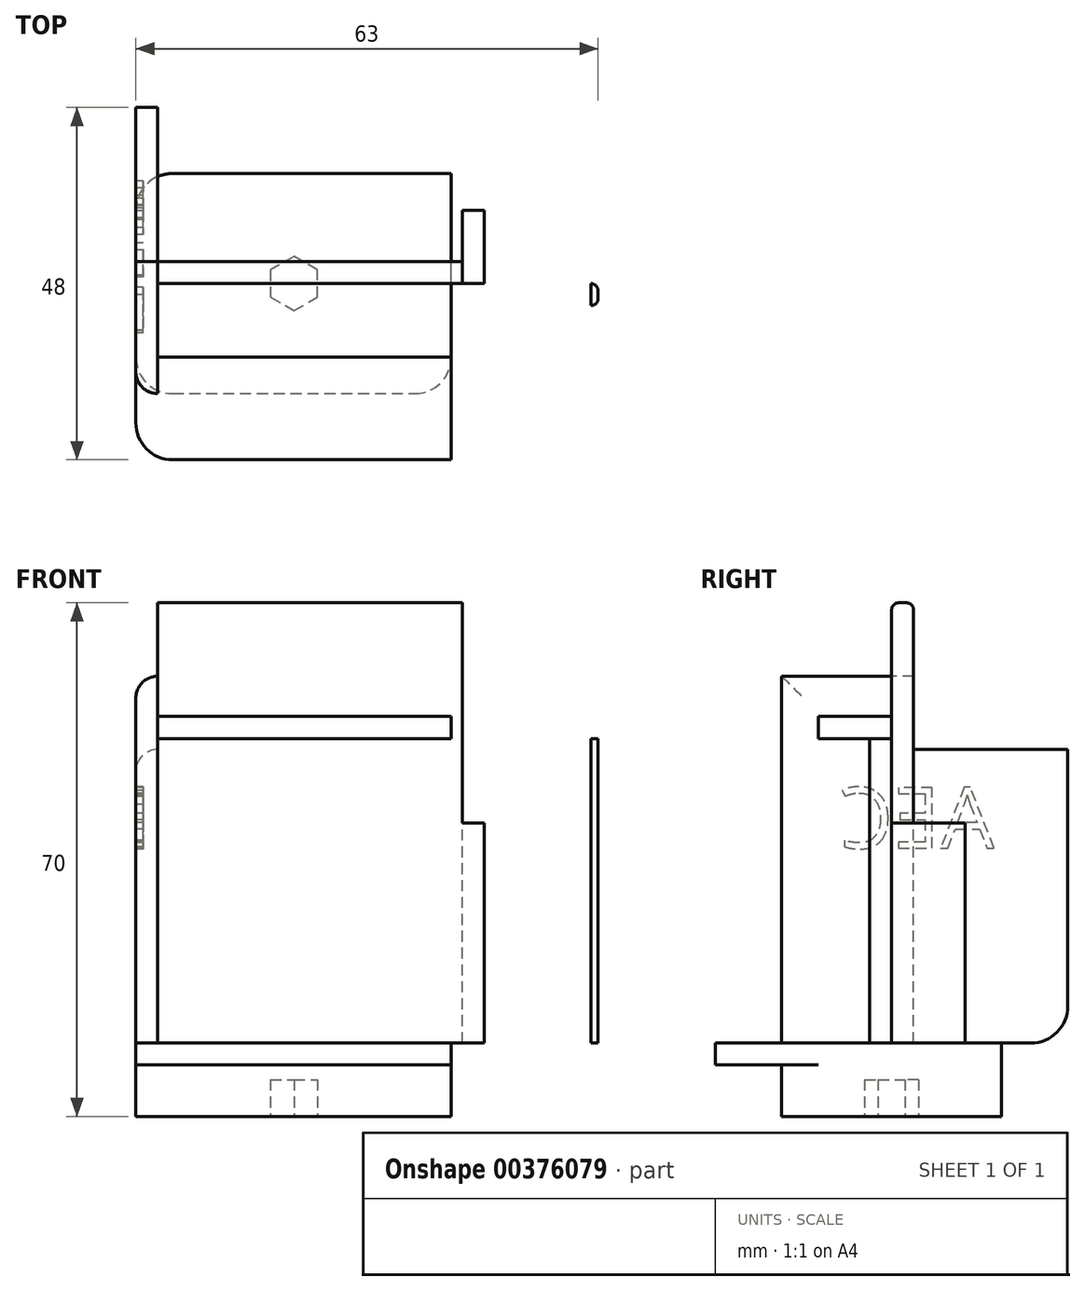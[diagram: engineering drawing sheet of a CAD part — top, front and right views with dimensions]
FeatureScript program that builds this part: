
annotation { "Feature Type Name" : "Feature", "Feature Type Description" : "" }
export const myFeature = defineFeature(function(context is Context, id is Id, definition is map)
    precondition{}
    {
        {
            var Q0;
            Q0=qCreatedBy(makeId("Front.planeOp"),FACE);
            var sketch = newSketch(context, id + "F0", { "sketchPlane" : qUnion([Q0])});
            skLineSegment(sketch, "E0.bottom", {"start": v(0, 0) * mm, "end": v(60, 0) * mm});
            skLineSegment(sketch, "E0.top", {"start": v(0, 41.5) * mm, "end": v(60, 41.5) * mm});
            skLineSegment(sketch, "E0.left", {"start": v(0, 0) * mm, "end": v(0, 41.5) * mm});
            skLineSegment(sketch, "E0.right", {"start": v(60, 0) * mm, "end": v(60, 41.5) * mm});
            skSolve(sketch);
        }
        {
            var Q0;
            Q0=makeQuery(id+"F0.imprint","IMPRINT",FACE,{"disambiguationData":[TD([[makeQuery(id+"F0.imprint","IMPRINT",EDGE,{"derivedFrom":sQuery(id+"F0.wireOp",EDGE,"E0.bottom")}),1.0]])]});
            extrude(context, id + "F1", {"entities" : qUnion([Q0]), "depth" : 3 * mm});
        }
        {
            var Q0;
            Q0=makeQuery(id+"F1.opExtrude","CAP_FACE",FACE,{"disambiguationData":[OSD([sQuery(id+"F0.wireOp",EDGE,"E0.bottom"),sQuery(id+"F0.wireOp",EDGE,"E0.top"),sQuery(id+"F0.wireOp",EDGE,"E0.left"),sQuery(id+"F0.wireOp",EDGE,"E0.right")])],"isStart":true});
            var sketch = newSketch(context, id + "F2", { "sketchPlane" : qUnion([Q0])});
            skLineSegment(sketch, "E1.bottom", {"start": v(0, 0) * mm, "end": v(-41.5, 0) * mm});
            skLineSegment(sketch, "E1.top", {"start": v(0, 60) * mm, "end": v(-41.5, 60) * mm});
            skLineSegment(sketch, "E1.left", {"start": v(0, 0) * mm, "end": v(0, 60) * mm});
            skLineSegment(sketch, "E1.right", {"start": v(-41.5, 0) * mm, "end": v(-41.5, 60) * mm});
            skSolve(sketch);
        }
        {
            var Q0;
            {var subQ0=sQuery(id+"F2.wireOp",EDGE,"E1.top");Q0=makeQuery(id+"F2.imprint","IMPRINT",FACE,{"disambiguationData":[TD([[makeQuery(id+"F2.imprint","IMPRINT",EDGE,{"derivedFrom":subQ0}),1.0]])]});}
            var Q1;
            {var subQ0=sQuery(id+"F2.wireOp",EDGE,"E1.bottom");Q1=makeQuery(id+"F2.imprint","IMPRINT",FACE,{"disambiguationData":[TD([[makeQuery(id+"F2.imprint","IMPRINT",EDGE,{"derivedFrom":subQ0}),-1.0]])]});}
            extrude(context, id + "F3", {"entities" : qUnion([Q0, Q1]), "operationType" : NewBodyOperationType.ADD, "depth" : 3 * mm});
        }
        {
            var Q0;
            Q0=makeQuery(id+"F3.boolean.opBoolean","MERGE",FACE,{"derivedFrom":[makeQuery(id+"F1.opExtrude","SWEPT_FACE",FACE,{"disambiguationData":[OSD([sQuery(id+"F0.wireOp",EDGE,"E0.left")])]}),makeQuery(id+"F3.opExtrude","SWEPT_FACE",FACE,{"disambiguationData":[OSD([sQuery(id+"F2.wireOp",EDGE,"E1.left")])]})]});
            var sketch = newSketch(context, id + "F4", { "sketchPlane" : qUnion([Q0])});
            skLineSegment(sketch, "E2", {"start": v(0, 0) * mm, "end": v(-15, 0) * mm, "construction": true});
            skLineSegment(sketch, "E3", {"start": v(-15, 0) * mm, "end": v(15, 0) * mm, "construction": true});
            skLineSegment(sketch, "E4", {"start": v(15, 0) * mm, "end": v(15, 50) * mm, "construction": true});
            skLineSegment(sketch, "E5.bottom", {"start": v(-15, 0) * mm, "end": v(15, 0) * mm});
            skLineSegment(sketch, "E5.top", {"start": v(-15, 50) * mm, "end": v(15, 50) * mm});
            skLineSegment(sketch, "E5.left", {"start": v(-15, 0) * mm, "end": v(-15, 50) * mm});
            skLineSegment(sketch, "E5.right", {"start": v(15, 0) * mm, "end": v(15, 50) * mm});
            skSolve(sketch);
        }
        {
            var Q0;
            {var subQ3=sQuery(id+"F4.wireOp",EDGE,"E5.left");Q0=makeQuery(id+"F4.imprint","IMPRINT",FACE,{"disambiguationData":[TD([[makeQuery(id+"F4.imprint","IMPRINT",EDGE,{"derivedFrom":subQ3}),-1.0]])]});}
            var Q1;
            {var subQ2=sQuery(id+"F4.wireOp",EDGE,"E5.right");Q1=makeQuery(id+"F4.imprint","IMPRINT",FACE,{"disambiguationData":[TD([[makeQuery(id+"F4.imprint","IMPRINT",EDGE,{"derivedFrom":subQ2}),1.0]])]});}
            var Q2;
            {var subQ0=sQuery(id+"F0.wireOp",EDGE,"E0.left");var subQ1=makeQuery(id+"F1.opExtrude","CAP_EDGE",EDGE,{"disambiguationData":[OSD([subQ0])],"isStart":false});Q2=makeQuery(id+"F4.imprint","IMPRINT",FACE,{"disambiguationData":[TD([[makeQuery(id+"F4.imprint","IMPRINT",EDGE,{"derivedFrom":subQ1}),1.0]])]});}
            extrude(context, id + "F5", {"entities" : qUnion([Q0, Q1, Q2]), "operationType" : NewBodyOperationType.ADD, "depth" : 3 * mm});
        }
        {
            var Q0;
            Q0=makeQuery(id+"F5.boolean.opBoolean","MERGE",FACE,{"derivedFrom":[makeQuery(id+"F3.boolean.opBoolean","MERGE",FACE,{"derivedFrom":[makeQuery(id+"F1.opExtrude","SWEPT_FACE",FACE,{"disambiguationData":[OSD([sQuery(id+"F0.wireOp",EDGE,"E0.bottom")])]}),makeQuery(id+"F3.opExtrude","SWEPT_FACE",FACE,{"disambiguationData":[OSD([sQuery(id+"F2.wireOp",EDGE,"E1.bottom")])]})]}),makeQuery(id+"F5.opExtrude","SWEPT_FACE",FACE,{"disambiguationData":[OSD([sQuery(id+"F4.wireOp",EDGE,"E5.bottom")])]})]});
            var sketch = newSketch(context, id + "F6", { "sketchPlane" : qUnion([Q0])});
            skLineSegment(sketch, "E6.bottom", {"start": v(-3, 15) * mm, "end": v(47, 15) * mm});
            skLineSegment(sketch, "E6.top", {"start": v(-3, -15) * mm, "end": v(47, -15) * mm});
            skLineSegment(sketch, "E6.left", {"start": v(-3, 15) * mm, "end": v(-3, -15) * mm});
            skLineSegment(sketch, "E6.right", {"start": v(47, 15) * mm, "end": v(47, -15) * mm});
            skSolve(sketch);
        }
        {
            var Q0;
            {var subQ0=sQuery(id+"F6.wireOp",EDGE,"E6.bottom");var subQ5=sQuery(id+"F6.wireOp",EDGE,"E6.right");var subQ6=makeQuery(id+"F6.imprint","INTERSECT",VERTEX,{"derivedFrom":[subQ0,subQ5]});Q0=makeQuery(id+"F6.imprint","IMPRINT",FACE,{"disambiguationData":[TD([[makeQuery(id+"F6.imprint","IMPRINT",EDGE,{"disambiguationData":[TD([[subQ6,-1.0]])],"derivedFrom":subQ5}),-1.0]])]});}
            var Q1;
            {var subQ0=sQuery(id+"F2.wireOp",EDGE,"E1.bottom");Q1=makeQuery(id+"F6.imprint","IMPRINT",FACE,{"disambiguationData":[TD([[makeQuery(id+"F6.imprint","IMPRINT",EDGE,{"derivedFrom":makeQuery(id+"F3.opExtrude","CAP_EDGE",EDGE,{"disambiguationData":[OSD([subQ0])],"isStart":false})}),-1.0]])]});}
            var Q2;
            {var subQ6=sQuery(id+"F6.wireOp",EDGE,"E6.left");Q2=makeQuery(id+"F6.imprint","IMPRINT",FACE,{"disambiguationData":[TD([[makeQuery(id+"F6.imprint","IMPRINT",EDGE,{"derivedFrom":subQ6}),-1.0]])]});}
            extrude(context, id + "F7", {"entities" : qUnion([Q0, Q1, Q2]), "operationType" : NewBodyOperationType.ADD, "depth" : 10 * mm});
        }
        {
            var Q0;
            Q0=makeQuery(id+"F7.boolean.opBoolean","MERGE",FACE,{"derivedFrom":[makeQuery(id+"F5.opExtrude","SWEPT_FACE",FACE,{"disambiguationData":[OSD([sQuery(id+"F4.wireOp",EDGE,"E5.right")])]}),makeQuery(id+"F7.opExtrude","SWEPT_FACE",FACE,{"disambiguationData":[OSD([sQuery(id+"F6.wireOp",EDGE,"E6.bottom")])]})]});
            var sketch = newSketch(context, id + "F8", { "sketchPlane" : qUnion([Q0])});
            skLineSegment(sketch, "E7.bottom", {"start": v(-3, 0) * mm, "end": v(47, 0) * mm});
            skLineSegment(sketch, "E7.top", {"start": v(-3, -3) * mm, "end": v(47, -3) * mm});
            skLineSegment(sketch, "E7.left", {"start": v(-3, 0) * mm, "end": v(-3, -3) * mm});
            skLineSegment(sketch, "E7.right", {"start": v(47, 0) * mm, "end": v(47, -3) * mm});
            skSolve(sketch);
        }
        {
            var Q0;
            Q0=makeQuery(id+"F8.imprint","IMPRINT",FACE,{"disambiguationData":[TD([[makeQuery(id+"F8.imprint","IMPRINT",EDGE,{"derivedFrom":sQuery(id+"F8.wireOp",EDGE,"E7.top")}),1.0]])]});
            extrude(context, id + "F9", {"entities" : qUnion([Q0]), "operationType" : NewBodyOperationType.ADD, "depth" : 9 * mm});
        }
        {
            var Q0;
            Q0=makeQuery(id+"F9.opExtrude","CAP_FACE",FACE,{"disambiguationData":[OSD([sQuery(id+"F8.wireOp",EDGE,"E7.bottom"),sQuery(id+"F8.wireOp",EDGE,"E7.top"),sQuery(id+"F8.wireOp",EDGE,"E7.left"),sQuery(id+"F8.wireOp",EDGE,"E7.right")])],"isStart":false});
            var sketch = newSketch(context, id + "F10", { "sketchPlane" : qUnion([Q0])});
            skLineSegment(sketch, "E8.bottom", {"start": v(22, -3) * mm, "end": v(47, -3) * mm});
            skLineSegment(sketch, "E8.top", {"start": v(22, 7) * mm, "end": v(47, 7) * mm});
            skLineSegment(sketch, "E8.left", {"start": v(22, -3) * mm, "end": v(22, 7) * mm});
            skLineSegment(sketch, "E8.right", {"start": v(47, -3) * mm, "end": v(47, 7) * mm});
            skSolve(sketch);
        }
        {
            var Q0;
            {var subQ0=sQuery(id+"F10.wireOp",EDGE,"E8.top");Q0=makeQuery(id+"F10.imprint","IMPRINT",FACE,{"disambiguationData":[TD([[makeQuery(id+"F10.imprint","IMPRINT",EDGE,{"derivedFrom":subQ0}),-1.0]])]});}
            var Q1;
            {var subQ0=sQuery(id+"F10.wireOp",EDGE,"E8.bottom");Q1=makeQuery(id+"F10.imprint","IMPRINT",FACE,{"disambiguationData":[TD([[makeQuery(id+"F10.imprint","IMPRINT",EDGE,{"derivedFrom":subQ0}),1.0]])]});}
            extrude(context, id + "F11", {"entities" : qUnion([Q0, Q1]), "operationType" : NewBodyOperationType.ADD, "depth" : 3 * mm});
        }
        {
            var Q0;
            Q0=makeQuery(id+"F11.opExtrude","CAP_FACE",FACE,{"disambiguationData":[OSD([sQuery(id+"F10.wireOp",EDGE,"E8.bottom"),sQuery(id+"F10.wireOp",EDGE,"E8.top"),sQuery(id+"F10.wireOp",EDGE,"E8.left"),sQuery(id+"F10.wireOp",EDGE,"E8.right")])],"isStart":false});
            var sketch = newSketch(context, id + "F12", { "sketchPlane" : qUnion([Q0])});
            skArc(sketch, "E9", {"start": v(17.11, 3.6) * mm, "mid": v(26.46, 3.05) * mm, "end": v(24.78, 12.26) * mm});
            skLineSegment(sketch, "E10", {"start": v(24.78, 12.26) * mm, "end": v(17.11, 3.6) * mm});
            skSolve(sketch);
        }
        {
            var Q0;
            {var subQ0=sQuery(id+"F12.wireOp",EDGE,"E9");var subQ1=makeQuery(id+"F11.opExtrude","CAP_EDGE",EDGE,{"disambiguationData":[OSD([sQuery(id+"F10.wireOp",EDGE,"E8.left")])],"isStart":false});var subQ2=makeQuery(id+"F12.imprint","INTERSECT",VERTEX,{"derivedFrom":[subQ1,subQ0]});Q0=makeQuery(id+"F12.imprint","IMPRINT",FACE,{"disambiguationData":[TD([[makeQuery(id+"F12.imprint","IMPRINT",EDGE,{"disambiguationData":[TD([[subQ2,-1.0]])],"derivedFrom":subQ0}),1.0]])]});}
            extrude(context, id + "F13", {"entities" : qUnion([Q0]), "operationType" : NewBodyOperationType.REMOVE, "oppositeDirection" : true, "depth" : 3 * mm});
        }
        {
            var Q0;
            Q0=makeQuery(id+"F11.boolean.opBoolean","MERGE",FACE,{"derivedFrom":[makeQuery(id+"F9.boolean.opBoolean","MERGE",FACE,{"derivedFrom":[makeQuery(id+"F7.opExtrude","SWEPT_FACE",FACE,{"disambiguationData":[OSD([sQuery(id+"F6.wireOp",EDGE,"E6.right")])]}),makeQuery(id+"F9.opExtrude","SWEPT_FACE",FACE,{"disambiguationData":[OSD([sQuery(id+"F8.wireOp",EDGE,"E7.right")])]})]}),makeQuery(id+"F11.opExtrude","SWEPT_FACE",FACE,{"disambiguationData":[OSD([sQuery(id+"F10.wireOp",EDGE,"E8.right")])]})]});
            var sketch = newSketch(context, id + "F14", { "sketchPlane" : qUnion([Q0])});
            skLineSegment(sketch, "E11.bottom", {"start": v(15, 0) * mm, "end": v(-27.93, 0) * mm});
            skLineSegment(sketch, "E11.top", {"start": v(15, -10) * mm, "end": v(-27.93, -10) * mm});
            skLineSegment(sketch, "E11.left", {"start": v(15, 0) * mm, "end": v(15, -10) * mm});
            skLineSegment(sketch, "E11.right", {"start": v(-27.93, 0) * mm, "end": v(-27.93, -10) * mm});
            skSolve(sketch);
        }
        {
            var Q0;
            {var subQ5=sQuery(id+"F14.wireOp",EDGE,"E11.left");Q0=makeQuery(id+"F14.imprint","IMPRINT",FACE,{"disambiguationData":[TD([[makeQuery(id+"F14.imprint","IMPRINT",EDGE,{"derivedFrom":subQ5}),1.0]])]});}
            var Q1;
            {var subQ3=sQuery(id+"F14.wireOp",EDGE,"E11.right");Q1=makeQuery(id+"F14.imprint","IMPRINT",FACE,{"disambiguationData":[TD([[makeQuery(id+"F14.imprint","IMPRINT",EDGE,{"derivedFrom":subQ3}),1.0]])]});}
            extrude(context, id + "F15", {"entities" : qUnion([Q0, Q1]), "operationType" : NewBodyOperationType.REMOVE, "oppositeDirection" : true, "depth" : 7 * mm});
        }
        {
            var Q0;
            Q0=makeQuery(id+"F11.boolean.opBoolean","MERGE",FACE,{"derivedFrom":[makeQuery(id+"F9.boolean.opBoolean","MERGE",FACE,{"derivedFrom":[makeQuery(id+"F7.opExtrude","SWEPT_FACE",FACE,{"disambiguationData":[OSD([sQuery(id+"F6.wireOp",EDGE,"E6.right")])]}),makeQuery(id+"F9.opExtrude","SWEPT_FACE",FACE,{"disambiguationData":[OSD([sQuery(id+"F8.wireOp",EDGE,"E7.right")])]})]}),makeQuery(id+"F11.opExtrude","SWEPT_FACE",FACE,{"disambiguationData":[OSD([sQuery(id+"F10.wireOp",EDGE,"E8.right")])]})]});
            var sketch = newSketch(context, id + "F16", { "sketchPlane" : qUnion([Q0])});
            skLineSegment(sketch, "E12.bottom", {"start": v(-31.9, 9.79) * mm, "end": v(-20.1, 9.79) * mm});
            skLineSegment(sketch, "E12.top", {"start": v(-31.9, -3.14) * mm, "end": v(-20.1, -3.14) * mm});
            skLineSegment(sketch, "E12.left", {"start": v(-31.9, 9.79) * mm, "end": v(-31.9, -3.14) * mm});
            skLineSegment(sketch, "E12.right", {"start": v(-20.1, 9.79) * mm, "end": v(-20.1, -3.14) * mm});
            skSolve(sketch);
        }
        {
            var Q0;
            {var subQ0=sQuery(id+"F10.wireOp",EDGE,"E8.right");Q0=makeQuery(id+"F16.imprint","IMPRINT",FACE,{"disambiguationData":[TD([[makeQuery(id+"F16.imprint","IMPRINT",EDGE,{"derivedFrom":makeQuery(id+"F11.opExtrude","CAP_EDGE",EDGE,{"disambiguationData":[OSD([subQ0])],"isStart":true})}),1.0]])]});}
            extrude(context, id + "F17", {"entities" : qUnion([Q0]), "operationType" : NewBodyOperationType.REMOVE, "oppositeDirection" : true, "depth" : 7 * mm});
        }
        {
            var Q0;
            Q0=makeQuery(id+"F11.opExtrude","CAP_FACE",FACE,{"disambiguationData":[OSD([sQuery(id+"F10.wireOp",EDGE,"E8.bottom"),sQuery(id+"F10.wireOp",EDGE,"E8.top"),sQuery(id+"F10.wireOp",EDGE,"E8.left"),sQuery(id+"F10.wireOp",EDGE,"E8.right")])],"isStart":false});
            var sketch = newSketch(context, id + "F18", { "sketchPlane" : qUnion([Q0])});
            skLineSegment(sketch, "E13.bottom", {"start": v(40, 7) * mm, "end": v(35.21, 7) * mm});
            skLineSegment(sketch, "E13.top", {"start": v(40, 2.28) * mm, "end": v(35.21, 2.28) * mm});
            skLineSegment(sketch, "E13.left", {"start": v(40, 7) * mm, "end": v(40, 2.28) * mm});
            skLineSegment(sketch, "E13.right", {"start": v(35.21, 7) * mm, "end": v(35.21, 2.28) * mm});
            skSolve(sketch);
        }
        {
            var Q0;
            Q0=makeQuery(id+"F18.imprint","IMPRINT",FACE,{"disambiguationData":[TD([[makeQuery(id+"F18.imprint","IMPRINT",EDGE,{"derivedFrom":sQuery(id+"F18.wireOp",EDGE,"E13.bottom")}),-1.0]])]});
            extrude(context, id + "F19", {"entities" : qUnion([Q0]), "operationType" : NewBodyOperationType.REMOVE, "oppositeDirection" : true, "depth" : 5 * mm});
        }
        {
            var Q0;
            Q0=makeQuery(id+"F1.opExtrude","SWEPT_FACE",FACE,{"disambiguationData":[OSD([sQuery(id+"F0.wireOp",EDGE,"E0.top")])]});
            var sketch = newSketch(context, id + "F20", { "sketchPlane" : qUnion([Q0])});
            skLineSegment(sketch, "E14.bottom", {"start": v(0, 0) * mm, "end": v(40, 0) * mm});
            skLineSegment(sketch, "E14.top", {"start": v(0, -10) * mm, "end": v(40, -10) * mm});
            skLineSegment(sketch, "E14.left", {"start": v(0, 0) * mm, "end": v(0, -10) * mm});
            skLineSegment(sketch, "E14.right", {"start": v(40, 0) * mm, "end": v(40, -10) * mm});
            skSolve(sketch);
        }
        {
            var Q0;
            {var subQ0=sQuery(id+"F20.wireOp",EDGE,"E14.top");Q0=makeQuery(id+"F20.imprint","IMPRINT",FACE,{"disambiguationData":[TD([[makeQuery(id+"F20.imprint","IMPRINT",EDGE,{"derivedFrom":subQ0}),1.0]])]});}
            var Q1;
            {var subQ0=sQuery(id+"F20.wireOp",EDGE,"E14.bottom");Q1=makeQuery(id+"F20.imprint","IMPRINT",FACE,{"disambiguationData":[TD([[makeQuery(id+"F20.imprint","IMPRINT",EDGE,{"derivedFrom":subQ0}),-1.0]])]});}
            extrude(context, id + "F21", {"entities" : qUnion([Q0, Q1]), "operationType" : NewBodyOperationType.ADD, "depth" : 3 * mm});
        }
        {
            var Q0;
            Q0=makeQuery(id+"F3.opExtrude","SWEPT_FACE",FACE,{"disambiguationData":[OSD([sQuery(id+"F2.wireOp",EDGE,"E1.right")])]});
            var sketch = newSketch(context, id + "F22", { "sketchPlane" : qUnion([Q0])});
            skLineSegment(sketch, "E15.bottom", {"start": v(0, 0) * mm, "end": v(10, 0) * mm});
            skLineSegment(sketch, "E15.top", {"start": v(0, 30) * mm, "end": v(10, 30) * mm});
            skLineSegment(sketch, "E15.left", {"start": v(0, 0) * mm, "end": v(0, 30) * mm});
            skLineSegment(sketch, "E15.right", {"start": v(10, 0) * mm, "end": v(10, 30) * mm});
            skSolve(sketch);
        }
        {
            var Q0;
            {var subQ3=sQuery(id+"F22.wireOp",EDGE,"E15.right");Q0=makeQuery(id+"F22.imprint","IMPRINT",FACE,{"disambiguationData":[TD([[makeQuery(id+"F22.imprint","IMPRINT",EDGE,{"derivedFrom":subQ3}),1.0]])]});}
            var Q1;
            {var subQ4=sQuery(id+"F22.wireOp",EDGE,"E15.left");Q1=makeQuery(id+"F22.imprint","IMPRINT",FACE,{"disambiguationData":[TD([[makeQuery(id+"F22.imprint","IMPRINT",EDGE,{"derivedFrom":subQ4}),-1.0]])]});}
            extrude(context, id + "F23", {"entities" : qUnion([Q0, Q1]), "operationType" : NewBodyOperationType.ADD, "depth" : 3 * mm});
        }
        {
            var Q0;
            Q0=makeQuery(id+"F7.boolean.opBoolean","MERGE",FACE,{"derivedFrom":[makeQuery(id+"F5.opExtrude","SWEPT_FACE",FACE,{"disambiguationData":[OSD([sQuery(id+"F4.wireOp",EDGE,"E5.left")])]}),makeQuery(id+"F7.opExtrude","SWEPT_FACE",FACE,{"disambiguationData":[OSD([sQuery(id+"F6.wireOp",EDGE,"E6.top")])]})]});
            var sketch = newSketch(context, id + "F24", { "sketchPlane" : qUnion([Q0])});
            skLineSegment(sketch, "E16.bottom", {"start": v(0, 50) * mm, "end": v(3, 50) * mm});
            skLineSegment(sketch, "E16.top", {"start": v(0, 0) * mm, "end": v(3, 0) * mm});
            skLineSegment(sketch, "E16.left", {"start": v(0, 50) * mm, "end": v(0, 0) * mm});
            skLineSegment(sketch, "E16.right", {"start": v(3, 50) * mm, "end": v(3, 0) * mm});
            skSolve(sketch);
        }
        {
            var Q0;
            Q0=makeQuery(id+"F24.imprint","IMPRINT",FACE,{"disambiguationData":[TD([[makeQuery(id+"F24.imprint","IMPRINT",EDGE,{"derivedFrom":sQuery(id+"F24.wireOp",EDGE,"E16.bottom")}),1.0]])]});
            extrude(context, id + "F25", {"entities" : qUnion([Q0]), "operationType" : NewBodyOperationType.ADD, "depth" : 9 * mm});
        }
        {
            var Q0;
            Q0=makeQuery(id+"F11.opExtrude","CAP_FACE",FACE,{"disambiguationData":[OSD([sQuery(id+"F10.wireOp",EDGE,"E8.bottom"),sQuery(id+"F10.wireOp",EDGE,"E8.top"),sQuery(id+"F10.wireOp",EDGE,"E8.left"),sQuery(id+"F10.wireOp",EDGE,"E8.right")])],"isStart":false});
            var sketch = newSketch(context, id + "F26", { "sketchPlane" : qUnion([Q0])});
            skLineSegment(sketch, "E17.bottom", {"start": v(27.95, 7) * mm, "end": v(22, 7) * mm});
            skLineSegment(sketch, "E17.top", {"start": v(27.95, 1.05) * mm, "end": v(22, 1.05) * mm});
            skLineSegment(sketch, "E17.left", {"start": v(27.95, 7) * mm, "end": v(27.95, 1.05) * mm});
            skLineSegment(sketch, "E17.right", {"start": v(22, 7) * mm, "end": v(22, 1.05) * mm});
            skSolve(sketch);
        }
        {
            var Q0;
            Q0=makeQuery(id+"F26.imprint","IMPRINT",FACE,{"disambiguationData":[TD([[makeQuery(id+"F26.imprint","IMPRINT",EDGE,{"derivedFrom":sQuery(id+"F26.wireOp",EDGE,"E17.top")}),-1.0]])]});
            extrude(context, id + "F27", {"entities" : qUnion([Q0]), "operationType" : NewBodyOperationType.REMOVE, "oppositeDirection" : true, "depth" : 5 * mm});
        }
        {
            var Q0;
            Q0=makeQuery(id+"F25.opExtrude","CAP_FACE",FACE,{"disambiguationData":[OSD([sQuery(id+"F24.wireOp",EDGE,"E16.bottom"),sQuery(id+"F24.wireOp",EDGE,"E16.top"),sQuery(id+"F24.wireOp",EDGE,"E16.left"),sQuery(id+"F24.wireOp",EDGE,"E16.right")])],"isStart":false});
            var sketch = newSketch(context, id + "F28", { "sketchPlane" : qUnion([Q0])});
            skLineSegment(sketch, "E18", {"start": v(0, 0) * mm, "end": v(0, 40) * mm, "construction": true});
            skLineSegment(sketch, "E19", {"start": v(0, 40) * mm, "end": v(-9.05, 40) * mm, "construction": true});
            skLineSegment(sketch, "E20.bottom", {"start": v(0, 40) * mm, "end": v(5.6, 40) * mm, "construction": true});
            skLineSegment(sketch, "E20.top", {"start": v(0, 52.74) * mm, "end": v(5.6, 52.74) * mm, "construction": true});
            skLineSegment(sketch, "E20.left", {"start": v(0, 40) * mm, "end": v(0, 52.74) * mm, "construction": true});
            skLineSegment(sketch, "E20.right", {"start": v(5.6, 40) * mm, "end": v(5.6, 52.74) * mm, "construction": true});
            skLineSegment(sketch, "E21.bottom", {"start": v(0, 40) * mm, "end": v(5.6, 40) * mm});
            skLineSegment(sketch, "E21.top", {"start": v(0, 52.74) * mm, "end": v(5.6, 52.74) * mm});
            skLineSegment(sketch, "E21.left", {"start": v(0, 40) * mm, "end": v(0, 52.74) * mm});
            skLineSegment(sketch, "E21.right", {"start": v(5.6, 40) * mm, "end": v(5.6, 52.74) * mm});
            skSolve(sketch);
        }
        {
            var Q0;
            {var subQ5=makeQuery(id+"F25.opExtrude","CAP_EDGE",EDGE,{"disambiguationData":[OSD([sQuery(id+"F24.wireOp",EDGE,"E16.bottom")])],"isStart":false});Q0=makeQuery(id+"F28.imprint","IMPRINT",FACE,{"disambiguationData":[TD([[makeQuery(id+"F28.imprint","IMPRINT",EDGE,{"derivedFrom":subQ5}),1.0]])]});}
            extrude(context, id + "F29", {"entities" : qUnion([Q0]), "operationType" : NewBodyOperationType.REMOVE, "oppositeDirection" : true, "depth" : 21 * mm});
        }
        {
            var Q0;
            Q0=makeQuery(id+"F25.opExtrude","CAP_FACE",FACE,{"disambiguationData":[OSD([sQuery(id+"F24.wireOp",EDGE,"E16.bottom"),sQuery(id+"F24.wireOp",EDGE,"E16.top"),sQuery(id+"F24.wireOp",EDGE,"E16.left"),sQuery(id+"F24.wireOp",EDGE,"E16.right")])],"isStart":false});
            var sketch = newSketch(context, id + "F30", { "sketchPlane" : qUnion([Q0])});
            skLineSegment(sketch, "E22", {"start": v(0, 0) * mm, "end": v(3, 0) * mm, "construction": true});
            skLineSegment(sketch, "E23", {"start": v(3, 0) * mm, "end": v(3, 40) * mm, "construction": true});
            skLineSegment(sketch, "E24.left", {"start": v(3, 40) * mm, "end": v(3, 22) * mm});
            skLineSegment(sketch, "E24.right", {"start": v(-7.41, 35.3) * mm, "end": v(-7.41, 26.8) * mm});
            skLineSegment(sketch, "E25.top", {"start": v(-7.41, 35.3) * mm, "end": v(-2.71, 35.3) * mm});
            skLineSegment(sketch, "E25.right", {"start": v(-2.71, 40) * mm, "end": v(-2.71, 35.3) * mm});
            skLineSegment(sketch, "E26.top", {"start": v(-7.41, 26.8) * mm, "end": v(-1.51, 26.8) * mm});
            skLineSegment(sketch, "E26.right", {"start": v(-1.51, 22) * mm, "end": v(-1.51, 26.8) * mm});
            skLineSegment(sketch, "E27", {"start": v(-2.71, 40) * mm, "end": v(3, 40) * mm});
            skLineSegment(sketch, "E28", {"start": v(-1.51, 22) * mm, "end": v(3, 22) * mm});
            skSolve(sketch);
        }
        {
            var Q0;
            {var subQ0=sQuery(id+"F30.wireOp",EDGE,"E24.left");Q0=makeQuery(id+"F30.imprint","IMPRINT",FACE,{"disambiguationData":[TD([[makeQuery(id+"F30.imprint","IMPRINT",EDGE,{"derivedFrom":subQ0}),1.0]])]});}
            var Q1;
            Q1=makeQuery(id+"F30.imprint","IMPRINT",FACE,{"disambiguationData":[TD([[makeQuery(id+"F30.imprint","IMPRINT",EDGE,{"derivedFrom":sQuery(id+"F30.wireOp",EDGE,"E24.right")}),1.0]])]});
            extrude(context, id + "F31", {"entities" : qUnion([Q0, Q1]), "operationType" : NewBodyOperationType.ADD, "depth" : 3 * mm});
        }
        {
            var Q0;
            Q0=makeQuery(id+"F31.opExtrude","CAP_EDGE",EDGE,{"disambiguationData":[OSD([sQuery(id+"F30.wireOp",EDGE,"E24.right")])],"isStart":false});
            fillet(context, id + "F32", {"entities" : qUnion([Q0]), "radius" : 1 * mm, "tangentPropagation" : true, "allowEdgeOverflow" : false});
        }
        {
            var Q0;
            Q0=makeQuery(id+"F31.opExtrude","CAP_EDGE",EDGE,{"disambiguationData":[OSD([sQuery(id+"F30.wireOp",EDGE,"E25.top")])],"isStart":false});
            var Q1;
            Q1=makeQuery(id+"F31.opExtrude","CAP_EDGE",EDGE,{"disambiguationData":[OSD([sQuery(id+"F30.wireOp",EDGE,"E26.top")])],"isStart":false});
            var Q2;
            Q2=makeQuery(id+"F31.opExtrude","CAP_EDGE",EDGE,{"disambiguationData":[OSD([sQuery(id+"F30.wireOp",EDGE,"E26.right")])],"isStart":false});
            var Q3;
            Q3=makeQuery(id+"F31.opExtrude","CAP_EDGE",EDGE,{"disambiguationData":[OSD([sQuery(id+"F30.wireOp",EDGE,"E25.right")])],"isStart":false});
            fillet(context, id + "F33", {"entities" : qUnion([Q0, Q1, Q2, Q3]), "radius" : 1 * mm, "tangentPropagation" : true, "allowEdgeOverflow" : false});
        }
        {
            var Q0;
            Q0=makeQuery(id+"F25.opExtrude","CAP_EDGE",EDGE,{"disambiguationData":[OSD([sQuery(id+"F24.wireOp",EDGE,"E16.top")])],"isStart":false});
            fillet(context, id + "F34", {"entities" : qUnion([Q0]), "radius" : 5 * mm, "tangentPropagation" : true, "allowEdgeOverflow" : false});
        }
        {
            var Q0;
            Q0=makeQuery(id+"F19.boolean.opBoolean","COPY",EDGE,{"derivedFrom":makeQuery(id+"F19.opExtrude","CAP_EDGE",EDGE,{"disambiguationData":[OSD([sQuery(id+"F18.wireOp",EDGE,"E13.right")])],"isStart":true})});
            var Q1;
            Q1=makeQuery(id+"F19.boolean.opBoolean","COPY",EDGE,{"derivedFrom":makeQuery(id+"F19.opExtrude","CAP_EDGE",EDGE,{"disambiguationData":[OSD([sQuery(id+"F18.wireOp",EDGE,"E13.top")])],"isStart":true})});
            var Q2;
            Q2=makeQuery(id+"F11.opExtrude","CAP_EDGE",EDGE,{"disambiguationData":[OSD([sQuery(id+"F10.wireOp",EDGE,"E8.top")])],"isStart":false});
            var Q3;
            Q3=makeQuery(id+"F27.boolean.opBoolean","COPY",EDGE,{"derivedFrom":makeQuery(id+"F27.opExtrude","CAP_EDGE",EDGE,{"disambiguationData":[OSD([sQuery(id+"F26.wireOp",EDGE,"E17.left")])],"isStart":true})});
            var Q4;
            Q4=makeQuery(id+"F27.boolean.opBoolean","COPY",EDGE,{"derivedFrom":makeQuery(id+"F27.opExtrude","CAP_EDGE",EDGE,{"disambiguationData":[OSD([sQuery(id+"F26.wireOp",EDGE,"E17.top")])],"isStart":true})});
            fillet(context, id + "F35", {"entities" : qUnion([Q0, Q1, Q2, Q3, Q4]), "radius" : 1 * mm, "tangentPropagation" : true, "allowEdgeOverflow" : false});
        }
        {
            var Q0;
            Q0=makeQuery(id+"F9.opExtrude","CAP_EDGE",EDGE,{"disambiguationData":[OSD([sQuery(id+"F8.wireOp",EDGE,"E7.left")])],"isStart":false});
            fillet(context, id + "F36", {"entities" : qUnion([Q0]), "radius" : 5 * mm, "tangentPropagation" : true, "allowEdgeOverflow" : false});
        }
        {
            var Q0;
            Q0=makeQuery(id+"F1.opExtrude","CAP_EDGE",EDGE,{"disambiguationData":[OSD([sQuery(id+"F0.wireOp",EDGE,"E0.right")])],"isStart":false});
            var Q1;
            Q1=makeQuery(id+"F1.opExtrude","CAP_EDGE",EDGE,{"disambiguationData":[OSD([sQuery(id+"F0.wireOp",EDGE,"E0.right")])],"isStart":true});
            fillet(context, id + "F37", {"entities" : qUnion([Q0, Q1]), "radius" : 1 * mm, "tangentPropagation" : true, "allowEdgeOverflow" : false});
        }
        {
            var Q0;
            Q0=makeQuery(id+"F3.opExtrude","CAP_EDGE",EDGE,{"disambiguationData":[OSD([sQuery(id+"F2.wireOp",EDGE,"E1.top")])],"isStart":false});
            var Q1;
            Q1=makeQuery(id+"F3.opExtrude","CAP_EDGE",EDGE,{"disambiguationData":[OSD([sQuery(id+"F2.wireOp",EDGE,"E1.top")])],"isStart":true});
            fillet(context, id + "F38", {"entities" : qUnion([Q0, Q1]), "radius" : 1 * mm, "tangentPropagation" : true, "allowEdgeOverflow" : false});
        }
        {
            var Q0;
            Q0=makeQuery(id+"F15.boolean.opBoolean","COPY",EDGE,{"derivedFrom":makeQuery(id+"F15.opExtrude","CAP_EDGE",EDGE,{"disambiguationData":[OSD([sQuery(id+"F14.wireOp",EDGE,"E11.left")])],"isStart":false})});
            var Q1;
            {var subQ0=sQuery(id+"F6.wireOp",EDGE,"E6.right");var subQ2=sQuery(id+"F6.wireOp",EDGE,"E6.bottom");var subQ3=sQuery(id+"F4.wireOp",EDGE,"E5.right");Q1=makeQuery(id+"F15.boolean.opBoolean","INTERSECT",EDGE,{"derivedFrom":[makeQuery(id+"F9.boolean.opBoolean","SPLIT",FACE,{"disambiguationData":[TD([makeQuery(id+"F7.opExtrude","SWEPT_FACE",FACE,{"disambiguationData":[OSD([subQ0])]})])],"derivedFrom":makeQuery(id+"F7.boolean.opBoolean","MERGE",FACE,{"derivedFrom":[makeQuery(id+"F5.opExtrude","SWEPT_FACE",FACE,{"disambiguationData":[OSD([subQ3])]}),makeQuery(id+"F7.opExtrude","SWEPT_FACE",FACE,{"disambiguationData":[OSD([subQ2])]})]})}),makeQuery(id+"F15.opExtrude","CAP_FACE",FACE,{"disambiguationData":[OSD([sQuery(id+"F14.wireOp",EDGE,"E11.bottom"),sQuery(id+"F14.wireOp",EDGE,"E11.top"),sQuery(id+"F14.wireOp",EDGE,"E11.left"),sQuery(id+"F14.wireOp",EDGE,"E11.right")])],"isStart":false})]});}
            var Q2;
            Q2=makeQuery(id+"F7.boolean.opBoolean","MERGE",EDGE,{"derivedFrom":[makeQuery(id+"F5.opExtrude","CAP_EDGE",EDGE,{"disambiguationData":[OSD([sQuery(id+"F4.wireOp",EDGE,"E5.left")])],"isStart":false}),makeQuery(id+"F7.opExtrude","SWEPT_EDGE",EDGE,{"disambiguationData":[OSD([sQuery(id+"F6.wireOp",EDGE,"E6.top"),sQuery(id+"F6.wireOp",EDGE,"E6.left")])]})]});
            var Q3;
            {var subQ0=sQuery(id+"F6.wireOp",EDGE,"E6.left");var subQ1=sQuery(id+"F6.wireOp",EDGE,"E6.bottom");var subQ2=sQuery(id+"F4.wireOp",EDGE,"E5.right");Q3=makeQuery(id+"F9.boolean.opBoolean","SPLIT",EDGE,{"disambiguationData":[TD([makeQuery(id+"F9.opExtrude","SWEPT_FACE",FACE,{"disambiguationData":[OSD([sQuery(id+"F8.wireOp",EDGE,"E7.top")])]})])],"derivedFrom":makeQuery(id+"F7.boolean.opBoolean","MERGE",EDGE,{"derivedFrom":[makeQuery(id+"F5.opExtrude","CAP_EDGE",EDGE,{"disambiguationData":[OSD([subQ2])],"isStart":false}),makeQuery(id+"F7.opExtrude","SWEPT_EDGE",EDGE,{"disambiguationData":[OSD([subQ1,subQ0])]})]})});}
            fillet(context, id + "F39", {"entities" : qUnion([Q0, Q1, Q2, Q3]), "radius" : 5 * mm, "tangentPropagation" : true, "allowEdgeOverflow" : false});
        }
        {
            var Q0;
            Q0=makeQuery(id+"F31.boolean.opBoolean","MERGE",FACE,{"derivedFrom":[makeQuery(id+"F25.boolean.opBoolean","MERGE",FACE,{"derivedFrom":[makeQuery(id+"F9.boolean.opBoolean","MERGE",FACE,{"derivedFrom":[makeQuery(id+"F7.boolean.opBoolean","MERGE",FACE,{"derivedFrom":[makeQuery(id+"F5.opExtrude","CAP_FACE",FACE,{"disambiguationData":[OSD([sQuery(id+"F4.wireOp",EDGE,"E5.bottom"),sQuery(id+"F4.wireOp",EDGE,"E5.top"),sQuery(id+"F4.wireOp",EDGE,"E5.left"),sQuery(id+"F4.wireOp",EDGE,"E5.right")])],"isStart":false}),makeQuery(id+"F7.opExtrude","SWEPT_FACE",FACE,{"disambiguationData":[OSD([sQuery(id+"F6.wireOp",EDGE,"E6.left")])]})]}),makeQuery(id+"F9.opExtrude","SWEPT_FACE",FACE,{"disambiguationData":[OSD([sQuery(id+"F8.wireOp",EDGE,"E7.left")])]})]}),makeQuery(id+"F25.opExtrude","SWEPT_FACE",FACE,{"disambiguationData":[OSD([sQuery(id+"F24.wireOp",EDGE,"E16.right")])]})]}),makeQuery(id+"F31.opExtrude","SWEPT_FACE",FACE,{"disambiguationData":[OSD([sQuery(id+"F30.wireOp",EDGE,"E24.left")])]})]});
            var sketch = newSketch(context, id + "F40", { "sketchPlane" : qUnion([Q0])});
            skText(sketch, "E29", { "text": "AEC", "fontName": "OpenSans-Regular.ttf"});
            const initialGuessF40  = {"E29": [-0.01398, 0.02655, 1, 0, 0.00833]};
            skSetInitialGuess(sketch, initialGuessF40);
            skSolve(sketch);
        }
        {
            var Q0;
            Q0=qSketchRegion(id+"F40",true);
            extrude(context, id + "F41", {"entities" : qUnion([Q0]), "operationType" : NewBodyOperationType.REMOVE, "oppositeDirection" : true, "depth" : 1 * mm});
        }
        {
            var Q0;
            Q0=makeQuery(id+"F7.opExtrude","CAP_FACE",FACE,{"disambiguationData":[OSD([sQuery(id+"F6.wireOp",EDGE,"E6.bottom"),sQuery(id+"F6.wireOp",EDGE,"E6.top"),sQuery(id+"F6.wireOp",EDGE,"E6.left"),sQuery(id+"F6.wireOp",EDGE,"E6.right")])],"isStart":false});
            var sketch = newSketch(context, id + "F42", { "sketchPlane" : qUnion([Q0])});
            skCircle(sketch, "E30.cCircle", {"center": v(18.55, 0) * mm, "radius": 3.2 * mm, "construction": true});
            skLineSegment(sketch, "E30.0", {"start": v(21.75, 1.85) * mm, "end": v(21.75, -1.85) * mm});
            skLineSegment(sketch, "E30.1", {"start": v(21.75, -1.85) * mm, "end": v(18.55, -3.7) * mm});
            skLineSegment(sketch, "E30.2", {"start": v(18.55, -3.7) * mm, "end": v(15.35, -1.85) * mm});
            skLineSegment(sketch, "E30.3", {"start": v(15.35, -1.85) * mm, "end": v(15.35, 1.85) * mm});
            skLineSegment(sketch, "E30.4", {"start": v(15.35, 1.85) * mm, "end": v(18.55, 3.7) * mm});
            skLineSegment(sketch, "E30.5", {"start": v(18.55, 3.7) * mm, "end": v(21.75, 1.85) * mm});
            skPoint(sketch, "E30.0.midPoint", {"position": v(21.75, 0) * mm});
            skSolve(sketch);
        }
        {
            var Q0;
            Q0=makeQuery(id+"F42.imprint","IMPRINT",FACE,{"disambiguationData":[TD([[makeQuery(id+"F42.imprint","IMPRINT",EDGE,{"derivedFrom":sQuery(id+"F42.wireOp",EDGE,"E30.0")}),-1.0]])]});
            extrude(context, id + "F43", {"entities" : qUnion([Q0]), "operationType" : NewBodyOperationType.REMOVE, "oppositeDirection" : true, "depth" : 5 * mm});
        }
        {
            var Q0;
            Q0=makeQuery(id+"F9.opExtrude","CAP_FACE",FACE,{"disambiguationData":[OSD([sQuery(id+"F8.wireOp",EDGE,"E7.bottom"),sQuery(id+"F8.wireOp",EDGE,"E7.top"),sQuery(id+"F8.wireOp",EDGE,"E7.left"),sQuery(id+"F8.wireOp",EDGE,"E7.right")])],"isStart":false});
            var sketch = newSketch(context, id + "F44", { "sketchPlane" : qUnion([Q0])});
            skLineSegment(sketch, "E31.bottom", {"start": v(17.1, 10.52) * mm, "end": v(46.84, 10.52) * mm});
            skLineSegment(sketch, "E31.top", {"start": v(17.1, -7.16) * mm, "end": v(46.84, -7.16) * mm});
            skLineSegment(sketch, "E31.left", {"start": v(17.1, 10.52) * mm, "end": v(17.1, -7.16) * mm});
            skLineSegment(sketch, "E31.right", {"start": v(46.84, 10.52) * mm, "end": v(46.84, -7.16) * mm});
            skSolve(sketch);
        }
        {
            var Q0;
            {var subQ1=sQuery(id+"F44.wireOp",EDGE,"E31.bottom");Q0=makeQuery(id+"F44.imprint","IMPRINT",FACE,{"disambiguationData":[TD([[makeQuery(id+"F44.imprint","IMPRINT",EDGE,{"derivedFrom":subQ1}),-1.0]])]});}
            extrude(context, id + "F45", {"entities" : qUnion([Q0]), "operationType" : NewBodyOperationType.REMOVE, "depth" : 25 * mm});
        }
        {
            var Q0;
            Q0=makeQuery(id+"F25.opExtrude","CAP_FACE",FACE,{"disambiguationData":[OSD([sQuery(id+"F24.wireOp",EDGE,"E16.bottom"),sQuery(id+"F24.wireOp",EDGE,"E16.top"),sQuery(id+"F24.wireOp",EDGE,"E16.left"),sQuery(id+"F24.wireOp",EDGE,"E16.right")])],"isStart":false});
            var sketch = newSketch(context, id + "F46", { "sketchPlane" : qUnion([Q0])});
            skLineSegment(sketch, "E32.bottom", {"start": v(-11.73, 42.88) * mm, "end": v(14.08, 42.88) * mm});
            skLineSegment(sketch, "E32.top", {"start": v(-11.73, 19.17) * mm, "end": v(14.08, 19.17) * mm});
            skLineSegment(sketch, "E32.left", {"start": v(-11.73, 42.88) * mm, "end": v(-11.73, 19.17) * mm});
            skLineSegment(sketch, "E32.right", {"start": v(14.08, 42.88) * mm, "end": v(14.08, 19.17) * mm});
            skSolve(sketch);
        }
        {
            var Q0;
            Q0=makeQuery(id+"F46.imprint","IMPRINT",FACE,{"disambiguationData":[TD([[makeQuery(id+"F46.imprint","IMPRINT",EDGE,{"derivedFrom":sQuery(id+"F46.wireOp",EDGE,"E32.bottom")}),-1.0]])]});
            extrude(context, id + "F47", {"entities" : qUnion([Q0]), "operationType" : NewBodyOperationType.REMOVE, "depth" : 25 * mm});
        }
        {
            var Q0;
            Q0=makeQuery(id+"F25.boolean.opBoolean","MERGE",EDGE,{"derivedFrom":[makeQuery(id+"F5.opExtrude","CAP_EDGE",EDGE,{"disambiguationData":[OSD([sQuery(id+"F4.wireOp",EDGE,"E5.top")])],"isStart":false}),makeQuery(id+"F25.opExtrude","SWEPT_EDGE",EDGE,{"disambiguationData":[OSD([sQuery(id+"F24.wireOp",EDGE,"E16.bottom"),sQuery(id+"F24.wireOp",EDGE,"E16.right")])]})]});
            var Q1;
            Q1=makeQuery(id+"F29.boolean.opBoolean","COPY",EDGE,{"derivedFrom":makeQuery(id+"F29.opExtrude","CAP_EDGE",EDGE,{"disambiguationData":[OSD([sQuery(id+"F24.wireOp",EDGE,"E16.right")])],"isStart":false})});
            var Q2;
            Q2=makeQuery(id+"F31.boolean.opBoolean","MERGE",EDGE,{"derivedFrom":[makeQuery(id+"F29.boolean.opBoolean","COPY",EDGE,{"derivedFrom":makeQuery(id+"F29.opExtrude","SWEPT_EDGE",EDGE,{"disambiguationData":[OSD([sQuery(id+"F24.wireOp",EDGE,"E16.right"),sQuery(id+"F28.wireOp",EDGE,"E21.bottom")])]})}),makeQuery(id+"F31.opExtrude","SWEPT_EDGE",EDGE,{"disambiguationData":[OSD([sQuery(id+"F30.wireOp",EDGE,"E24.left"),sQuery(id+"F30.wireOp",EDGE,"E27")])]})]});
            var Q3;
            {var subQ0=sQuery(id+"F6.wireOp",EDGE,"E6.bottom");var subQ1=sQuery(id+"F4.wireOp",EDGE,"E5.right");var subQ2=sQuery(id+"F4.wireOp",EDGE,"E5.top");var subQ3=sQuery(id+"F6.wireOp",EDGE,"E6.left");Q3=makeQuery(id+"F9.boolean.opBoolean","SPLIT",EDGE,{"disambiguationData":[TD([makeQuery(id+"F5.opExtrude","SWEPT_FACE",FACE,{"disambiguationData":[OSD([subQ2])]})])],"derivedFrom":makeQuery(id+"F7.boolean.opBoolean","MERGE",EDGE,{"derivedFrom":[makeQuery(id+"F5.opExtrude","CAP_EDGE",EDGE,{"disambiguationData":[OSD([subQ1])],"isStart":false}),makeQuery(id+"F7.opExtrude","SWEPT_EDGE",EDGE,{"disambiguationData":[OSD([subQ0,subQ3])]})]})});}
            fillet(context, id + "F48", {"entities" : qUnion([Q0, Q1, Q2, Q3]), "radius" : 3 * mm, "tangentPropagation" : true, "allowEdgeOverflow" : false});
        }
        {
            var Q0;
            Q0=makeQuery(id+"F1.opExtrude","CAP_FACE",FACE,{"disambiguationData":[OSD([sQuery(id+"F0.wireOp",EDGE,"E0.bottom"),sQuery(id+"F0.wireOp",EDGE,"E0.top"),sQuery(id+"F0.wireOp",EDGE,"E0.left"),sQuery(id+"F0.wireOp",EDGE,"E0.right")])],"isStart":false});
            var sketch = newSketch(context, id + "F49", { "sketchPlane" : qUnion([Q0])});
            skLineSegment(sketch, "E33.bottom", {"start": v(0, 0) * mm, "end": v(65.18, 0) * mm});
            skLineSegment(sketch, "E33.top", {"start": v(0, 41.5) * mm, "end": v(65.18, 41.5) * mm});
            skLineSegment(sketch, "E33.left", {"start": v(0, 0) * mm, "end": v(0, 41.5) * mm});
            skLineSegment(sketch, "E33.right", {"start": v(65.18, 0) * mm, "end": v(65.18, 41.5) * mm});
            skSolve(sketch);
        }
        {
            var Q0;
            {var subQ4=sQuery(id+"F49.wireOp",EDGE,"E33.left");Q0=makeQuery(id+"F49.imprint","IMPRINT",FACE,{"disambiguationData":[TD([[makeQuery(id+"F49.imprint","IMPRINT",EDGE,{"derivedFrom":subQ4}),-1.0]])]});}
            extrude(context, id + "F50", {"entities" : qUnion([Q0]), "operationType" : NewBodyOperationType.REMOVE, "oppositeDirection" : true, "depth" : 3 * mm});
        }
    });
